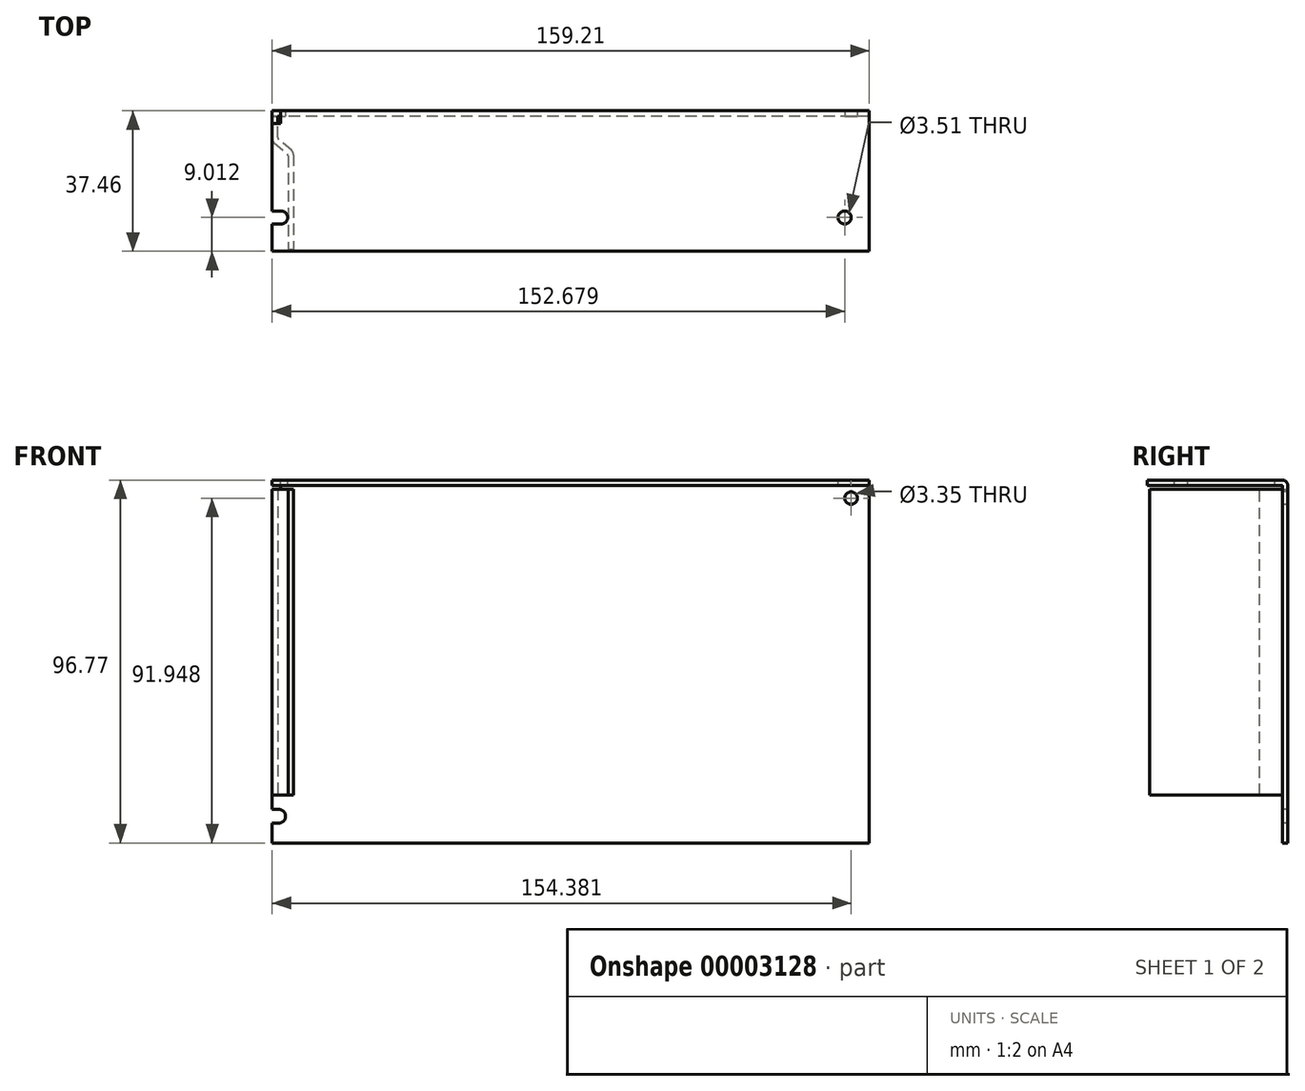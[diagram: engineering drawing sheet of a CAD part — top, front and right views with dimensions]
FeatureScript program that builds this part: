
annotation { "Feature Type Name" : "Feature", "Feature Type Description" : "" }
export const myFeature = defineFeature(function(context is Context, id is Id, definition is map)
    precondition{}
    {
        {
            var Q0;
            Q0=qCreatedBy(makeId("Right.planeOp"),FACE);
            var sketch = newSketch(context, id + "F0", { "sketchPlane" : qUnion([Q0])});
            skLineSegment(sketch, "E0", {"start": v(0, 95.25) * mm, "end": v(0, 0) * mm});
            skLineSegment(sketch, "E1", {"start": v(-1.52, 96.77) * mm, "end": v(-37.47, 96.77) * mm});
            skPoint(sketch, "E2.visualSharp", {"position": v(0, 96.77) * mm});
            skArc(sketch, "E2.filletArc", {"start": v(0, 95.25) * mm, "mid": v(-0.45, 96.33) * mm, "end": v(-1.52, 96.77) * mm});
            skLineSegment(sketch, "E3.0", {"start": v(-1.52, 95.33) * mm, "end": v(-37.47, 95.33) * mm});
            skArc(sketch, "E3.1", {"start": v(-1.45, 95.25) * mm, "mid": v(-1.47, 95.3) * mm, "end": v(-1.52, 95.33) * mm});
            skLineSegment(sketch, "E3.2", {"start": v(-1.45, 95.25) * mm, "end": v(-1.45, 0) * mm});
            skLineSegment(sketch, "E4", {"start": v(-37.47, 96.77) * mm, "end": v(-37.47, 95.33) * mm});
            skLineSegment(sketch, "E5", {"start": v(-1.45, 0) * mm, "end": v(0, 0) * mm});
            skSolve(sketch);
        }
        {
            var Q0;
            Q0=makeQuery(id+"F0.imprint","IMPRINT",FACE,{"disambiguationData":[TD([[makeQuery(id+"F0.imprint","IMPRINT",EDGE,{"derivedFrom":sQuery(id+"F0.wireOp",EDGE,"E0")}),-1.0]])]});
            extrude(context, id + "F1", {"entities" : qUnion([Q0]), "depth" : 159.2 * mm});
        }
        {
            var Q0;
            Q0=makeQuery(id+"F1.opExtrude","SWEPT_FACE",FACE,{"disambiguationData":[OSD([sQuery(id+"F0.wireOp",EDGE,"E3.2")])]});
            var sketch = newSketch(context, id + "F2", { "sketchPlane" : qUnion([Q0])});
            skCircle(sketch, "E6", {"center": v(154.38, 91.95) * mm, "radius": 1.68 * mm});
            skArc(sketch, "E7", {"start": v(1.73, 5.28) * mm, "mid": v(3.56, 7.11) * mm, "end": v(1.73, 8.94) * mm});
            skLineSegment(sketch, "E8", {"start": v(0, 96.77) * mm, "end": v(165.87, 96.77) * mm, "construction": true});
            skLineSegment(sketch, "E9", {"start": v(1.73, 5.28) * mm, "end": v(0, 5.28) * mm});
            skLineSegment(sketch, "E10", {"start": v(1.73, 8.94) * mm, "end": v(0, 8.94) * mm});
            skLineSegment(sketch, "E11", {"start": v(0, 8.94) * mm, "end": v(0, 5.28) * mm});
            skSolve(sketch);
        }
        {
            var Q0;
            {Q0=qUnion([makeQuery(id+"F2.imprint","IMPRINT",FACE,{"disambiguationData":[TD([[makeQuery(id+"F2.imprint","IMPRINT",EDGE,{"derivedFrom":sQuery(id+"F2.wireOp",EDGE,"E6")}),1.0]])]}),makeQuery(id+"F2.imprint","IMPRINT",FACE,{"disambiguationData":[TD([[makeQuery(id+"F2.imprint","IMPRINT",EDGE,{"derivedFrom":sQuery(id+"F2.wireOp",EDGE,"E7")}),1.0]])]})]);}
            extrude(context, id + "F3", {"entities" : qUnion([Q0]), "operationType" : NewBodyOperationType.REMOVE, "endBound" : BoundingType.THROUGH_ALL, "oppositeDirection" : true, "depth" : 25.4 * mm});
        }
        {
            var Q0;
            Q0=makeQuery(id+"F1.opExtrude","SWEPT_FACE",FACE,{"disambiguationData":[OSD([sQuery(id+"F0.wireOp",EDGE,"E1")])]});
            var sketch = newSketch(context, id + "F4", { "sketchPlane" : qUnion([Q0])});
            skArc(sketch, "E12", {"start": v(2.36, -30.2) * mm, "mid": v(4.11, -28.45) * mm, "end": v(2.36, -26.7) * mm});
            skCircle(sketch, "E13", {"center": v(152.68, -28.45) * mm, "radius": 1.75 * mm});
            skLineSegment(sketch, "E14", {"start": v(2.36, -26.7) * mm, "end": v(0, -26.7) * mm});
            skLineSegment(sketch, "E15", {"start": v(2.36, -30.2) * mm, "end": v(0, -30.2) * mm});
            skLineSegment(sketch, "E16", {"start": v(0, -30.2) * mm, "end": v(0, -26.7) * mm});
            skSolve(sketch);
        }
        {
            var Q0;
            {Q0=qUnion([makeQuery(id+"F4.imprint","IMPRINT",FACE,{"disambiguationData":[TD([[makeQuery(id+"F4.imprint","IMPRINT",EDGE,{"derivedFrom":sQuery(id+"F4.wireOp",EDGE,"E12")}),1.0]])]}),makeQuery(id+"F4.imprint","IMPRINT",FACE,{"disambiguationData":[TD([[makeQuery(id+"F4.imprint","IMPRINT",EDGE,{"derivedFrom":sQuery(id+"F4.wireOp",EDGE,"E13")}),1.0]])]})]);}
            extrude(context, id + "F5", {"entities" : qUnion([Q0]), "operationType" : NewBodyOperationType.REMOVE, "endBound" : BoundingType.UP_TO_NEXT, "oppositeDirection" : true, "depth" : 25.4 * mm});
        }
        {
            var Q0;
            Q0=makeQuery(id+"F1.opExtrude","SWEPT_FACE",FACE,{"disambiguationData":[OSD([sQuery(id+"F0.wireOp",EDGE,"E3.2")])]});
            var sketch = newSketch(context, id + "F6", { "sketchPlane" : qUnion([Q0])});
            skLineSegment(sketch, "E17.bottom", {"start": v(0, 94.34) * mm, "end": v(1.45, 94.34) * mm});
            skLineSegment(sketch, "E17.top", {"start": v(0, 12.8) * mm, "end": v(1.45, 12.8) * mm});
            skLineSegment(sketch, "E17.left", {"start": v(0, 94.34) * mm, "end": v(0, 12.8) * mm});
            skLineSegment(sketch, "E17.right", {"start": v(1.45, 94.34) * mm, "end": v(1.45, 12.8) * mm});
            skSolve(sketch);
        }
        {
            var Q0;
            Q0=makeQuery(id+"F6.imprint","IMPRINT",FACE,{"disambiguationData":[TD([[makeQuery(id+"F6.imprint","IMPRINT",EDGE,{"derivedFrom":sQuery(id+"F6.wireOp",EDGE,"E17.bottom")}),-1.0]])]});
            extrude(context, id + "F7", {"entities" : qUnion([Q0]), "operationType" : NewBodyOperationType.ADD, "depth" : 6.1 * mm});
        }
        {
            var Q0;
            {var subQ0=sQuery(id+"F0.wireOp",EDGE,"E0");var subQ1=sQuery(id+"F0.wireOp",EDGE,"E1");var subQ2=sQuery(id+"F0.wireOp",EDGE,"E2.filletArc");var subQ3=sQuery(id+"F0.wireOp",EDGE,"E3.0");var subQ4=sQuery(id+"F0.wireOp",EDGE,"E3.1");var subQ5=sQuery(id+"F0.wireOp",EDGE,"E3.2");var subQ6=sQuery(id+"F0.wireOp",EDGE,"E4");var subQ11=makeQuery(id+"F1.opExtrude","SWEPT_FACE",FACE,{"disambiguationData":[OSD([subQ1])]});var subQ13=makeQuery(id+"F1.opExtrude","SWEPT_FACE",FACE,{"disambiguationData":[OSD([subQ0])]});Q0=makeQuery(id+"F7.boolean.opBoolean","MERGE",FACE,{"derivedFrom":[makeQuery(id+"F5.boolean.opBoolean","SPLIT",FACE,{"disambiguationData":[TD([subQ13])],"derivedFrom":makeQuery(id+"F3.boolean.opBoolean","SPLIT",FACE,{"disambiguationData":[TD([subQ11])],"derivedFrom":makeQuery(id+"F1.opExtrude","CAP_FACE",FACE,{"disambiguationData":[OSD([subQ0,subQ1,subQ2,subQ3,subQ4,subQ5,subQ6,sQuery(id+"F0.wireOp",EDGE,"E5")])],"isStart":true})})}),makeQuery(id+"F7.opExtrude","SWEPT_FACE",FACE,{"disambiguationData":[OSD([sQuery(id+"F6.wireOp",EDGE,"E17.left")])]})]});}
            var sketch = newSketch(context, id + "F8", { "sketchPlane" : qUnion([Q0])});
            skLineSegment(sketch, "E18.bottom", {"start": v(0, 94.34) * mm, "end": v(3.4, 94.34) * mm});
            skLineSegment(sketch, "E18.top", {"start": v(1.52, 96.77) * mm, "end": v(3.4, 96.77) * mm});
            skLineSegment(sketch, "E18.left", {"start": v(0, 94.34) * mm, "end": v(0, 95.25) * mm});
            skLineSegment(sketch, "E18.right", {"start": v(3.4, 94.34) * mm, "end": v(3.4, 96.77) * mm});
            skPoint(sketch, "E19.visualSharp", {"position": v(0, 96.77) * mm});
            skArc(sketch, "E19.filletArc", {"start": v(1.52, 96.77) * mm, "mid": v(0.45, 96.33) * mm, "end": v(0, 95.25) * mm});
            skSolve(sketch);
        }
        {
            var Q0;
            {var subQ2=sQuery(id+"F0.wireOp",EDGE,"E3.1");var subQ12=makeQuery(id+"F1.opExtrude","CAP_EDGE",EDGE,{"disambiguationData":[OSD([subQ2])],"isStart":true});var subQ20=makeQuery(id+"F8.imprint","IMPRINT",EDGE,{"derivedFrom":subQ12});var subQ26=sQuery(id+"F8.wireOp",EDGE,"E18.top");Q0=qUnion([makeQuery(id+"F8.imprint","IMPRINT",FACE,{"disambiguationData":[TD([[subQ20,-1.0]])]}),makeQuery(id+"F8.imprint","IMPRINT",FACE,{"disambiguationData":[TD([[makeQuery(id+"F8.imprint","IMPRINT",EDGE,{"derivedFrom":subQ26}),-1.0]])]})]);}
            extrude(context, id + "F9", {"entities" : qUnion([Q0]), "operationType" : NewBodyOperationType.REMOVE, "oppositeDirection" : true, "depth" : 2.3 * mm});
        }
        {
            var Q0;
            Q0=makeQuery(id+"F7.opExtrude","SWEPT_FACE",FACE,{"disambiguationData":[OSD([sQuery(id+"F6.wireOp",EDGE,"E17.top")])]});
            var sketch = newSketch(context, id + "F10", { "sketchPlane" : qUnion([Q0])});
            skLineSegment(sketch, "E20", {"start": v(5.66, 11.72) * mm, "end": v(5.66, 36.9) * mm});
            skLineSegment(sketch, "E21", {"start": v(4.22, 12.04) * mm, "end": v(4.22, 36.9) * mm});
            skLineSegment(sketch, "E22", {"start": v(4.22, 36.9) * mm, "end": v(5.66, 36.9) * mm});
            skPoint(sketch, "E23.visualSharp", {"position": v(5.66, 11) * mm});
            skPoint(sketch, "E24.visualSharp", {"position": v(4.22, 11.68) * mm});
            skLineSegment(sketch, "E25", {"start": v(5.12, 10.55) * mm, "end": v(1.72, 7.7) * mm});
            skLineSegment(sketch, "E26", {"start": v(0, 6.62) * mm, "end": v(0, 7.44) * mm});
            skLineSegment(sketch, "E27", {"start": v(0.54, 8.6) * mm, "end": v(3.94, 11.46) * mm});
            skLineSegment(sketch, "E28", {"start": v(0, 6.62) * mm, "end": v(1.45, 6.62) * mm});
            skLineSegment(sketch, "E29", {"start": v(1.45, 6.62) * mm, "end": v(1.45, 7.12) * mm});
            skPoint(sketch, "E30.visualSharp", {"position": v(0, 8.15) * mm});
            skArc(sketch, "E30.filletArc", {"start": v(0.54, 8.6) * mm, "mid": v(0.14, 8.08) * mm, "end": v(0, 7.44) * mm});
            skPoint(sketch, "E31.visualSharp", {"position": v(1.45, 7.47) * mm});
            skArc(sketch, "E31.filletArc", {"start": v(1.72, 7.7) * mm, "mid": v(1.52, 7.44) * mm, "end": v(1.45, 7.12) * mm});
            skArc(sketch, "E32.filletArc", {"start": v(3.94, 11.46) * mm, "mid": v(4.15, 11.72) * mm, "end": v(4.22, 12.04) * mm});
            skArc(sketch, "E33.filletArc", {"start": v(5.12, 10.55) * mm, "mid": v(5.52, 11.08) * mm, "end": v(5.66, 11.72) * mm});
            skSolve(sketch);
        }
        {
            var Q0;
            {var subQ11=sQuery(id+"F10.wireOp",EDGE,"E26");Q0=qUnion([makeQuery(id+"F10.imprint","IMPRINT",FACE,{"disambiguationData":[TD([[makeQuery(id+"F10.imprint","IMPRINT",EDGE,{"derivedFrom":sQuery(id+"F10.wireOp",EDGE,"E20")}),1.0]])]}),makeQuery(id+"F10.imprint","IMPRINT",FACE,{"disambiguationData":[TD([[makeQuery(id+"F10.imprint","IMPRINT",EDGE,{"derivedFrom":subQ11}),1.0]])]})]);}
            var Q1;
            Q1=makeQuery(id+"F9.boolean.opBoolean","MERGE",FACE,{"derivedFrom":[makeQuery(id+"F7.opExtrude","SWEPT_FACE",FACE,{"disambiguationData":[OSD([sQuery(id+"F6.wireOp",EDGE,"E17.bottom")])]}),makeQuery(id+"F9.opExtrude","SWEPT_FACE",FACE,{"disambiguationData":[OSD([sQuery(id+"F8.wireOp",EDGE,"E18.bottom")])]})]});
            extrude(context, id + "F11", {"entities" : qUnion([Q0]), "operationType" : NewBodyOperationType.ADD, "endBound" : BoundingType.UP_TO_SURFACE, "oppositeDirection" : true, "endBoundEntityFace" : qUnion([Q1]), "depth" : 25.4 * mm});
        }
    });
